# Revit family: BMDS_Mardome TRADE SV (1a)
name_source: partatom
category: Windows
revit_build: Autodesk Revit 2018 (Build: 20170223_1515(x64)
units: mm (PartAtom-declared; Revit-internal decimal feet)

## family parameters
Cut with Voids When Loaded = No
Host = Face
OmniClass Number = 23.30.30.00
OmniClass Title = Skylights
Room Calculation Point = No
Shared = No

## types (1)
- MARDOME
    AerodynamicFreeArea_Aa = 0 m²
    AerodynamicFreeArea_Cv = 0
    AssetType = Fixed
    BIMObjectName = BrettMartin_RooflightSystem_Mardome
    BREApprovedEnvironmentalProfileEcopointScore = 0
    BRECertifiedEnvironmentalProfileEmbodiedCarbon = 0.00 kg/m²
    BREGreenGuideRating = TBC
    BUpstand to DSurfaceOff = 63 mm
    Builders Upstand Check = 365 mm  [stored 1.19751 ft]
    Builders Upstand Height = 225 mm  [stored 0.738189 ft]
    Category = Pr_70_65_82_64
    Certification = CE marked to BS EN 12101-2 :2003; DoP ref: CE-SMV-001
    CodePerformance = To BS EN 12101-2 : 2003
    Construction Type = Mardome TRADE SV
    DFRO = 0 m²
    DFSAa = 0 m²
    DFSCv = 0
    DFWAa = 0 m²
    DFWCv = 0
    Default Elevation = 0 mm  [stored 0 ft]
    Description = Mardome TRADE Smoke Vent Rooflight
    DocumentReference = http://www.brettmartin.com
    Documentation = http://www.brettmartin.com
    Dome = Yes
    Dome Height = 95 mm
    Dome Pyramid = BMDS_natural clear
    Dome Pyramid Height = 95 mm
    Dome Surface Offset = 63 mm
    Dome/Pyramid = Dome
    DriveMechanism = Factory fitted 24V electrical actuator, to fully open in ≤60 seconds
    DurationUnit = year
    ExpectedLife = 20
    FFactor = 0.8
    Features = Various layer options
    FireRating = BROOF(t4) to EN13501-5 & Class B-s1,d0 to EN13501-1
    FragilityClass = To be Class B non-fragile to ACR[M]001 when fully fixed.
    FreeArea = 0 m²
    GlazingInner = Single Skin Inner
    GlazingOption = Textured Double Skin
    GlazingOuter = 3mm Marlon FSX Polycarbonate
    GlazingType = 3
    GrossArea = 1.44 m²
    GrossVolume = 0.75 m³
    Height = 523 mm
    IfcExportAs = IfcWindowStyle
    IfcExportType = SKYLIGHT
    Infiltration = 0
    Initiation = Automatic device activated by a signal from the fire alarm – optional Control Panel System with either a Fire Switch; Fireman’s Priority Switch or Smoke Detector
    Inner Frame = UHMW, White
    InstallationInstructions = To be fully fixed in accordance with BMDS fixing recommendations - see Technical Bulletin 286.
    IsExternal = Yes
    IsWired = Yes
    Kerb Type = 2
    KerbOption = Tall Kerb
    KerbType = 2
    KerbWind = 12
    Layername = BrettMartin_Mardome
    Length = 1200 mm  [stored 3.93701 ft]
    LowAmbientTemperatureClassification = T (-15)
    Manufacturer = Brett Martin Daylight Systems Ltd
    ManufacturerURL = http://www.brettmartin.com
    Material = Polycarbonate
    MethodOfMeasurement = BrettMartin_Mardome
    ModelLabel = BrettMartin_Mardome
    NBSDescription = Powered smoke and heat exhaust ventilators
    NBSReference = 90-45-30/370
    Name = Mardome TRADE SV
    NetVolume = 135 m³
    NominalHeight = 523 mm
    NominalLength = 1200 mm  [stored 3.93701 ft]
    NominalWidth = 1200 mm  [stored 3.93701 ft]
    NonOpenable = No
    O&MManual = BMDS COSHH 12 -  Mardome Product Safety & Handling COSHH Data Sheet
    Opening Length = 1200 mm  [stored 3.93701 ft]
    Opening Width = 1200 mm  [stored 3.93701 ft]
    Perimeter = 4800 mm
    PowerSupplyOptions = Without Control Panel - 24V DC / Control Panel - 230V AC/1.2A max, output supply 24-28V DC with max load 5A OR 8A.  See Technical Bulletin 286 for further details
    PredefinedType = BrettMartin_Mardome
    Process = Replacement at service life intervals
    Pyramid Height = 95 mm
    Reflectivity = 0
    ReliabilityClassification = Re 1000
    ResistanceToHeatClassification = B 300
    RoofOpeningArea = 0 m²
    SeviceLifeDuration = 20
    ShadingCoefficient = 0
    SmokeStop = No
    SnowLoadClassification = SL 500
    SolarAbsorption = 0
    SolarReflectance = 0
    SolarTransmittance = 0
    SystemManufacturer = Brett Martin Daylight Systems Ltd
    TCheck = 0
    TKRO = 0 m²
    TKSAa = 0 m²
    TKSCv = 0
    TKWAa = 0 m²
    TKWCv = 0
    ThermalTransmittance = 2.7
    TotalSolarTransmittance (GValue) = 0
    URL = http://www.brettmartin.com
    UV Protection = Co-extruded UV surface protection.
    Uniclass2015Code = Pr_70_65_82_64
    Uniclass2015Title = Powered smoke and heat exhaust ventilators
    Upstand = UHMW, White
    VentilationOpeningAngleSmokeModule = 140.00°
    Version = 1.0
    VisibleLightReflectance = 0
    VisibleLightTransmittance = 0.78
    Visual Light Transmittance = 0.78
    WarrantyDurationUnit = year
    WeightInner = 0.00 kg/m²
    WeightOuter = 0.00 kg/m²
    Width = 1200 mm  [stored 3.93701 ft]
    WidthLength = 0
    WindDeflector = Yes
    WindDeflectorOption = 10
    WindDeflectorSide = 460 mm
    WindDeflectorYes/No = Yes
    WindLoadClassification = WL 1500

note: [stored X ft] marks values corroborated as IEEE doubles in the binary element streams (Revit-internal decimal feet)

## geometry (parser evidence)
native form markers: Sweep x17
no freeform markers — native parametric forms only
